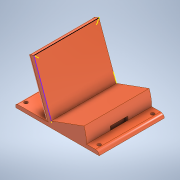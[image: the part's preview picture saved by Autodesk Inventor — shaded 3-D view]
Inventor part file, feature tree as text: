
AUTODESK INVENTOR PART (.ipt)
format: ipt  version: 2020 (Build 240168000, 168)  size: 364,032 bytes
history: native  units: in
note: dims shown in document units (in); Inventor stores cm internally (conversion verified against a paired STEP export)
features: sketch x7, extrude x4, fillet x2, revolve x1
ambient origin geometry x8: Origin, YZ Plane, XZ Plane, XY Plane, X Axis, Y Axis, Z Axis, Center Point
bodies: Solid1 (feature_tree)
feature tree (14):
  extrude  "Extrusion1"  Depth=0.1181in
  revolve  "Revolution1"  [1 undecoded]
  extrude  "Extrusion2"  Depth=0.25in
  extrude  "Extrusion3"  Depth=0.25in
  extrude  "Extrusion4"  Depth=0.1181in
  fillet  "Fillet1"  Radius=0.1181in
  fillet  "Fillet2"  Radius=0.2953in
  sketch  "Sketch6"  dims[d18=0.25in d19=0.0in]
  sketch  "Sketch7"  dims[d20=2.0866in d21=0.2953in d22=0.1181in d23=0.2953in d24=0.25in d25=0.0in d26=0.125in d27=0.06in]
  sketch  "Sketch1"  dims[d0=1.1024in d4=0.1181in]
  sketch  "Sketch2"  dims[d6=0.1181in d7=0.125in d8=0.0in]
  sketch  "Sketch3"  dims[d9=1.1811in d10=0.25in]
  sketch  "Sketch4"  dims[d11=0.1374in d12=0.25in]
  sketch  "Sketch5"  dims[d13=1.7323in d14=0.0in d15=0.2953in d16=0.1181in d17=0.2953in]
note: 1 required parameter value undecoded (feature->parameter linkage not recoverable at this tier; creation-order binding heuristic only, values carry confidence <= 0.55)
